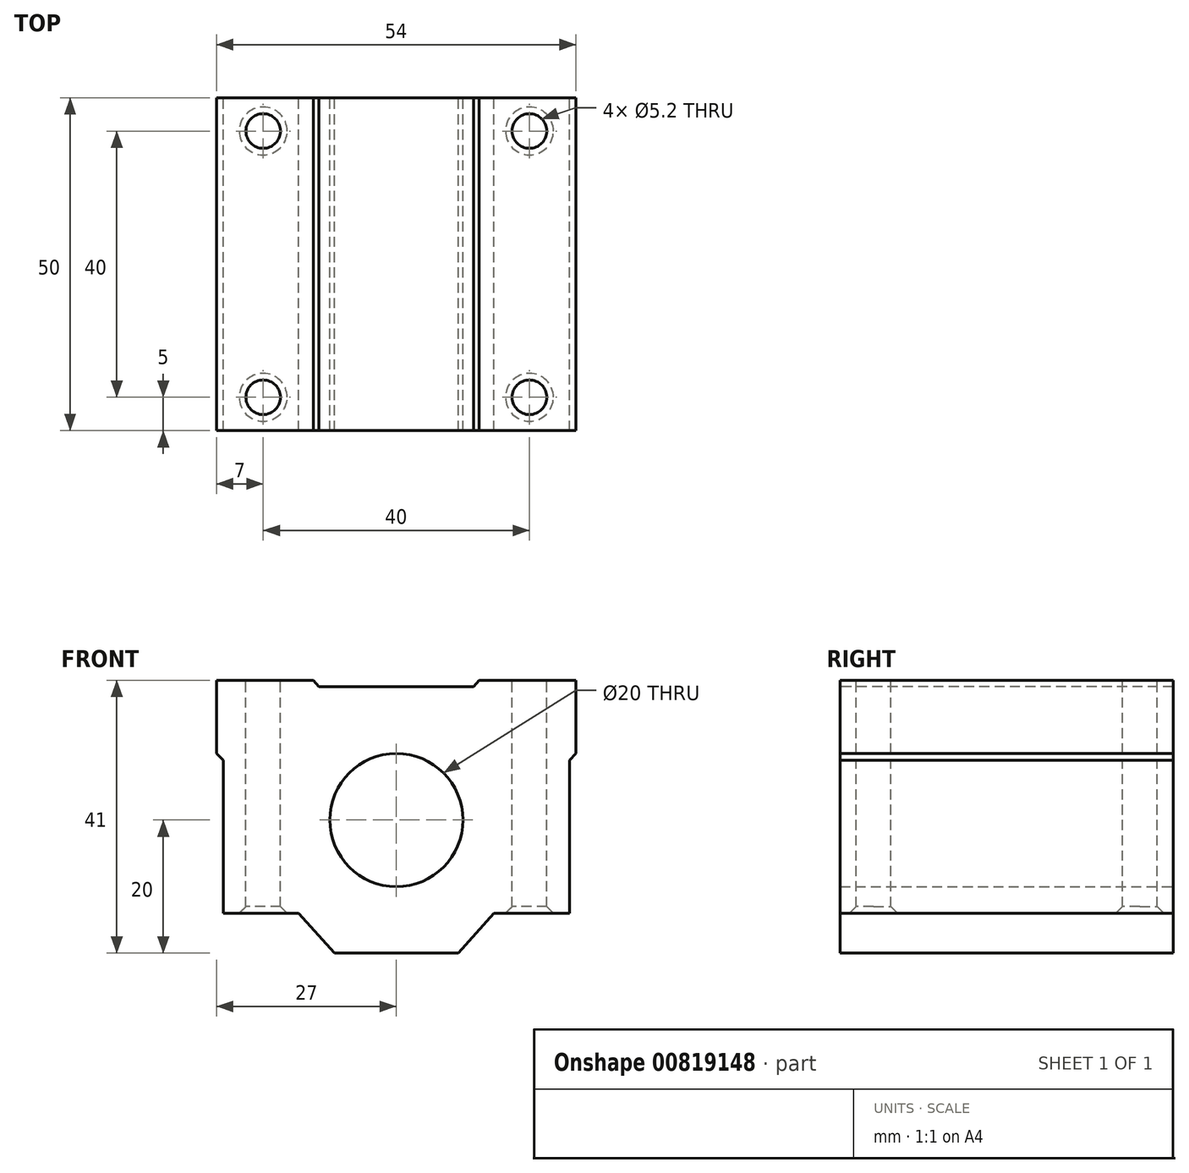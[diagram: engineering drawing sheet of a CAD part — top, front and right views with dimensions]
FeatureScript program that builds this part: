
annotation { "Feature Type Name" : "Feature", "Feature Type Description" : "" }
export const myFeature = defineFeature(function(context is Context, id is Id, definition is map)
    precondition{}
    {
        {
            var Q0;
            Q0=qCreatedBy(makeId("Front.planeOp"),FACE);
            var sketch = newSketch(context, id + "F0", { "sketchPlane" : qUnion([Q0])});
            skCircle(sketch, "E0", {"center": v(0, 0) * mm, "radius": 10 * mm});
            skLineSegment(sketch, "E1.rect.bottom", {"start": v(27, 21) * mm, "end": v(-27, 21) * mm});
            skLineSegment(sketch, "E1.rect.top", {"start": v(27, -20) * mm, "end": v(-27, -20) * mm});
            skLineSegment(sketch, "E1.rect.left", {"start": v(27, 21) * mm, "end": v(27, -20) * mm});
            skLineSegment(sketch, "E1.rect.right", {"start": v(-27, 21) * mm, "end": v(-27, -20) * mm});
            skPoint(sketch, "E1.rect.middle", {"position": v(0, 0.5) * mm});
            skLineSegment(sketch, "E2.0", {"start": v(27, 10) * mm, "end": v(-27, 10) * mm});
            skLineSegment(sketch, "E3.0", {"start": v(27, 9) * mm, "end": v(-27, 9) * mm});
            skLineSegment(sketch, "E4.0", {"start": v(27, -14) * mm, "end": v(-27, -14) * mm});
            skLineSegment(sketch, "E5.0", {"start": v(-26, 21) * mm, "end": v(-26, -20) * mm});
            skLineSegment(sketch, "E6.0", {"start": v(26, 21) * mm, "end": v(26, -20) * mm});
            skLineSegment(sketch, "E7", {"start": v(27, 10) * mm, "end": v(26, 9) * mm});
            skLineSegment(sketch, "E8", {"start": v(-27, 10) * mm, "end": v(-26, 9) * mm});
            skLineSegment(sketch, "E9", {"start": v(-14.67, -14) * mm, "end": v(-9.3, -20) * mm});
            skLineSegment(sketch, "E10.MirrorCS", {"start": v(14.67, -14) * mm, "end": v(9.3, -20) * mm});
            skPoint(sketch, "E11.orphan", {"position": v(16.75, -11.68) * mm});
            skPoint(sketch, "E12.orphan", {"position": v(5.82, -23.9) * mm});
            skPoint(sketch, "E13.orphan", {"position": v(-5.82, -23.9) * mm});
            skPoint(sketch, "E14.orphan", {"position": v(-16.75, -11.68) * mm});
            skSolve(sketch);
        }
        {
            var Q0;
            {var subQ3=sQuery(id+"F0.wireOp",EDGE,"E1.rect.bottom");var subQ5=sQuery(id+"F0.wireOp",EDGE,"E1.rect.left");var subQ7=makeQuery(id+"F0.imprint","INTERSECT",VERTEX,{"derivedFrom":[subQ3,subQ5]});Q0=makeQuery(id+"F0.imprint","IMPRINT",FACE,{"disambiguationData":[TD([[makeQuery(id+"F0.imprint","IMPRINT",EDGE,{"disambiguationData":[TD([[subQ7,-1.0]])],"derivedFrom":subQ3}),1.0]])]});}
            var Q1;
            {var subQ3=sQuery(id+"F0.wireOp",EDGE,"E1.rect.bottom");var subQ5=sQuery(id+"F0.wireOp",EDGE,"E1.rect.right");var subQ7=makeQuery(id+"F0.imprint","INTERSECT",VERTEX,{"derivedFrom":[subQ3,subQ5]});Q1=makeQuery(id+"F0.imprint","IMPRINT",FACE,{"disambiguationData":[TD([[makeQuery(id+"F0.imprint","IMPRINT",EDGE,{"disambiguationData":[TD([[subQ7,1.0]])],"derivedFrom":subQ3}),1.0]])]});}
            var Q2;
            {var subQ1=sQuery(id+"F0.wireOp",EDGE,"E9");Q2=makeQuery(id+"F0.imprint","IMPRINT",FACE,{"disambiguationData":[TD([[makeQuery(id+"F0.imprint","IMPRINT",EDGE,{"derivedFrom":subQ1}),1.0]])]});}
            var Q3;
            {var subQ0=sQuery(id+"F0.wireOp",EDGE,"E7");Q3=makeQuery(id+"F0.imprint","IMPRINT",FACE,{"disambiguationData":[TD([[makeQuery(id+"F0.imprint","IMPRINT",EDGE,{"derivedFrom":subQ0}),-1.0]])]});}
            var Q4;
            {var subQ0=sQuery(id+"F0.wireOp",EDGE,"E8");Q4=makeQuery(id+"F0.imprint","IMPRINT",FACE,{"disambiguationData":[TD([[makeQuery(id+"F0.imprint","IMPRINT",EDGE,{"derivedFrom":subQ0}),1.0]])]});}
            var Q5;
            {var subQ3=sQuery(id+"F0.wireOp",EDGE,"E3.0");var subQ10=sQuery(id+"F0.wireOp",EDGE,"E0");var subQ11=makeQuery(id+"F0.imprint","INTERSECT",VERTEX,{"disambiguationData":[OD(0.0)],"derivedFrom":[subQ10,subQ3]});Q5=makeQuery(id+"F0.imprint","IMPRINT",FACE,{"disambiguationData":[TD([[makeQuery(id+"F0.imprint","IMPRINT",EDGE,{"disambiguationData":[TD([[subQ11,1.0]])],"derivedFrom":subQ10}),-1.0]])]});}
            var Q6;
            {var subQ1=sQuery(id+"F0.wireOp",EDGE,"E0");var subQ5=sQuery(id+"F0.wireOp",EDGE,"E2.0");var subQ7=makeQuery(id+"F0.imprint","INTERSECT",VERTEX,{"derivedFrom":[subQ1,subQ5]});Q6=makeQuery(id+"F0.imprint","IMPRINT",FACE,{"disambiguationData":[TD([[makeQuery(id+"F0.imprint","IMPRINT",EDGE,{"disambiguationData":[TD([[subQ7,-1.0]])],"derivedFrom":subQ1}),-1.0]])]});}
            var Q7;
            {var subQ3=sQuery(id+"F0.wireOp",EDGE,"E1.rect.bottom");var subQ5=sQuery(id+"F0.wireOp",EDGE,"E5.0");var subQ6=makeQuery(id+"F0.imprint","INTERSECT",VERTEX,{"derivedFrom":[subQ3,subQ5]});Q7=makeQuery(id+"F0.imprint","IMPRINT",FACE,{"disambiguationData":[TD([[makeQuery(id+"F0.imprint","IMPRINT",EDGE,{"disambiguationData":[TD([[subQ6,1.0]])],"derivedFrom":subQ3}),1.0]])]});}
            var Q8;
            {var subQ1=sQuery(id+"F0.wireOp",EDGE,"E0");var subQ5=sQuery(id+"F0.wireOp",EDGE,"E2.0");var subQ7=makeQuery(id+"F0.imprint","INTERSECT",VERTEX,{"derivedFrom":[subQ1,subQ5]});Q8=makeQuery(id+"F0.imprint","IMPRINT",FACE,{"disambiguationData":[TD([[makeQuery(id+"F0.imprint","IMPRINT",EDGE,{"disambiguationData":[TD([[subQ7,1.0]])],"derivedFrom":subQ1}),-1.0]])]});}
            extrude(context, id + "F1", {"entities" : qUnion([Q0, Q1, Q2, Q3, Q4, Q5, Q6, Q7, Q8]), "depth" : 50 * mm, "symmetric" : true});
        }
        {
            var Q0;
            Q0=qCreatedBy(makeId("Front.planeOp"),FACE);
            var sketch = newSketch(context, id + "F2", { "sketchPlane" : qUnion([Q0])});
            skLineSegment(sketch, "E15.0", {"start": v(27, 21) * mm, "end": v(-27, 21) * mm});
            skLineSegment(sketch, "E16.0", {"start": v(27, 20) * mm, "end": v(-27, 20) * mm});
            skLineSegment(sketch, "E17", {"start": v(-11.6, 20) * mm, "end": v(-12.44, 21) * mm});
            skLineSegment(sketch, "E18.MirrorCS", {"start": v(11.6, 20) * mm, "end": v(12.44, 21) * mm});
            skPoint(sketch, "E19.orphan", {"position": v(13.28, 22) * mm});
            skPoint(sketch, "E20.orphan", {"position": v(10.73, 18.95) * mm});
            skPoint(sketch, "E21.orphan", {"position": v(-10.73, 18.95) * mm});
            skPoint(sketch, "E22.orphan", {"position": v(-13.28, 22) * mm});
            skSolve(sketch);
        }
        {
            var Q0;
            Q0=qSketchRegion(id+"F2",true);
            extrude(context, id + "F3", {"entities" : qUnion([Q0]), "operationType" : NewBodyOperationType.REMOVE, "oppositeDirection" : true, "depth" : 100 * mm, "symmetric" : true});
        }
        {
            var Q0;
            Q0=makeQuery(id+"F1.opExtrude","SWEPT_FACE",FACE,{"disambiguationData":[OSD([sQuery(id+"F0.wireOp",EDGE,"E1.rect.bottom")])]});
            var sketch = newSketch(context, id + "F4", { "sketchPlane" : qUnion([Q0])});
            skLineSegment(sketch, "E23.rect.bottom", {"start": v(20, 20) * mm, "end": v(-20, 20) * mm, "construction": true});
            skLineSegment(sketch, "E23.rect.top", {"start": v(20, -20) * mm, "end": v(-20, -20) * mm, "construction": true});
            skLineSegment(sketch, "E23.rect.left", {"start": v(20, 20) * mm, "end": v(20, -20) * mm, "construction": true});
            skLineSegment(sketch, "E23.rect.right", {"start": v(-20, 20) * mm, "end": v(-20, -20) * mm, "construction": true});
            skPoint(sketch, "E23.rect.middle", {"position": v(0, 0) * mm});
            skCircle(sketch, "E24", {"center": v(-20, -20) * mm, "radius": 2.6 * mm});
            skCircle(sketch, "E25", {"center": v(-20, 20) * mm, "radius": 2.6 * mm});
            skCircle(sketch, "E26", {"center": v(20, 20) * mm, "radius": 2.6 * mm});
            skCircle(sketch, "E27", {"center": v(20, -20) * mm, "radius": 2.6 * mm});
            skSolve(sketch);
        }
        {
            var Q0;
            Q0=makeQuery(id+"F4.imprint","IMPRINT",FACE,{"disambiguationData":[TD([[makeQuery(id+"F4.imprint","IMPRINT",EDGE,{"derivedFrom":sQuery(id+"F4.wireOp",EDGE,"E26")}),1.0]])]});
            var Q1;
            Q1=makeQuery(id+"F4.imprint","IMPRINT",FACE,{"disambiguationData":[TD([[makeQuery(id+"F4.imprint","IMPRINT",EDGE,{"derivedFrom":sQuery(id+"F4.wireOp",EDGE,"E25")}),1.0]])]});
            var Q2;
            Q2=makeQuery(id+"F4.imprint","IMPRINT",FACE,{"disambiguationData":[TD([[makeQuery(id+"F4.imprint","IMPRINT",EDGE,{"derivedFrom":sQuery(id+"F4.wireOp",EDGE,"E24")}),1.0]])]});
            var Q3;
            Q3=makeQuery(id+"F4.imprint","IMPRINT",FACE,{"disambiguationData":[TD([[makeQuery(id+"F4.imprint","IMPRINT",EDGE,{"derivedFrom":sQuery(id+"F4.wireOp",EDGE,"E27")}),1.0]])]});
            extrude(context, id + "F5", {"entities" : qUnion([Q0, Q1, Q2, Q3]), "operationType" : NewBodyOperationType.REMOVE, "endBound" : BoundingType.THROUGH_ALL, "oppositeDirection" : true, "depth" : 25 * mm});
        }
        {
            var Q0;
            Q0=makeQuery(id+"F5.boolean.opBoolean","COPY",EDGE,{"derivedFrom":makeQuery(id+"F5.opExtrude","CAP_EDGE",EDGE,{"disambiguationData":[OSD([sQuery(id+"F4.wireOp",EDGE,"E27")])],"isStart":true})});
            var Q1;
            Q1=makeQuery(id+"F5.boolean.opBoolean","COPY",EDGE,{"derivedFrom":makeQuery(id+"F5.opExtrude","CAP_EDGE",EDGE,{"disambiguationData":[OSD([sQuery(id+"F4.wireOp",EDGE,"E24")])],"isStart":true})});
            var Q2;
            Q2=makeQuery(id+"F5.boolean.opBoolean","COPY",EDGE,{"derivedFrom":makeQuery(id+"F5.opExtrude","CAP_EDGE",EDGE,{"disambiguationData":[OSD([sQuery(id+"F4.wireOp",EDGE,"E25")])],"isStart":true})});
            var Q3;
            Q3=makeQuery(id+"F5.boolean.opBoolean","COPY",EDGE,{"derivedFrom":makeQuery(id+"F5.opExtrude","CAP_EDGE",EDGE,{"disambiguationData":[OSD([sQuery(id+"F4.wireOp",EDGE,"E26")])],"isStart":true})});
            var Q4;
            {var subQ0=sQuery(id+"F0.wireOp",EDGE,"E4.0");Q4=makeQuery(id+"F5.boolean.opBoolean","INTERSECT",EDGE,{"derivedFrom":[makeQuery(id+"F1.opExtrude","SWEPT_FACE",FACE,{"disambiguationData":[OSD([subQ0]),TDD([makeQuery(id+"F0.imprint","IMPRINT",EDGE,{"disambiguationData":[TD([[makeQuery(id+"F0.imprint","INTERSECT",VERTEX,{"derivedFrom":[subQ0,sQuery(id+"F0.wireOp",EDGE,"E10.MirrorCS")]}),1.0]])],"derivedFrom":subQ0})])]}),makeQuery(id+"F5.opExtrude","SWEPT_FACE",FACE,{"disambiguationData":[OSD([sQuery(id+"F4.wireOp",EDGE,"E26")])]})]});}
            var Q5;
            {var subQ0=sQuery(id+"F0.wireOp",EDGE,"E4.0");Q5=makeQuery(id+"F5.boolean.opBoolean","INTERSECT",EDGE,{"derivedFrom":[makeQuery(id+"F1.opExtrude","SWEPT_FACE",FACE,{"disambiguationData":[OSD([subQ0]),TDD([makeQuery(id+"F0.imprint","IMPRINT",EDGE,{"disambiguationData":[TD([[makeQuery(id+"F0.imprint","INTERSECT",VERTEX,{"derivedFrom":[subQ0,sQuery(id+"F0.wireOp",EDGE,"E9")]}),-1.0]])],"derivedFrom":subQ0})])]}),makeQuery(id+"F5.opExtrude","SWEPT_FACE",FACE,{"disambiguationData":[OSD([sQuery(id+"F4.wireOp",EDGE,"E25")])]})]});}
            var Q6;
            {var subQ0=sQuery(id+"F0.wireOp",EDGE,"E4.0");Q6=makeQuery(id+"F5.boolean.opBoolean","INTERSECT",EDGE,{"derivedFrom":[makeQuery(id+"F1.opExtrude","SWEPT_FACE",FACE,{"disambiguationData":[OSD([subQ0]),TDD([makeQuery(id+"F0.imprint","IMPRINT",EDGE,{"disambiguationData":[TD([[makeQuery(id+"F0.imprint","INTERSECT",VERTEX,{"derivedFrom":[subQ0,sQuery(id+"F0.wireOp",EDGE,"E10.MirrorCS")]}),1.0]])],"derivedFrom":subQ0})])]}),makeQuery(id+"F5.opExtrude","SWEPT_FACE",FACE,{"disambiguationData":[OSD([sQuery(id+"F4.wireOp",EDGE,"E27")])]})]});}
            var Q7;
            {var subQ0=sQuery(id+"F0.wireOp",EDGE,"E4.0");Q7=makeQuery(id+"F5.boolean.opBoolean","INTERSECT",EDGE,{"derivedFrom":[makeQuery(id+"F1.opExtrude","SWEPT_FACE",FACE,{"disambiguationData":[OSD([subQ0]),TDD([makeQuery(id+"F0.imprint","IMPRINT",EDGE,{"disambiguationData":[TD([[makeQuery(id+"F0.imprint","INTERSECT",VERTEX,{"derivedFrom":[subQ0,sQuery(id+"F0.wireOp",EDGE,"E9")]}),-1.0]])],"derivedFrom":subQ0})])]}),makeQuery(id+"F5.opExtrude","SWEPT_FACE",FACE,{"disambiguationData":[OSD([sQuery(id+"F4.wireOp",EDGE,"E24")])]})]});}
            chamfer(context, id + "F6", {"entities" : qUnion([Q0, Q1, Q2, Q3, Q4, Q5, Q6, Q7]), "width" : 1 * mm, "tangentPropagation" : true});
        }
    });
